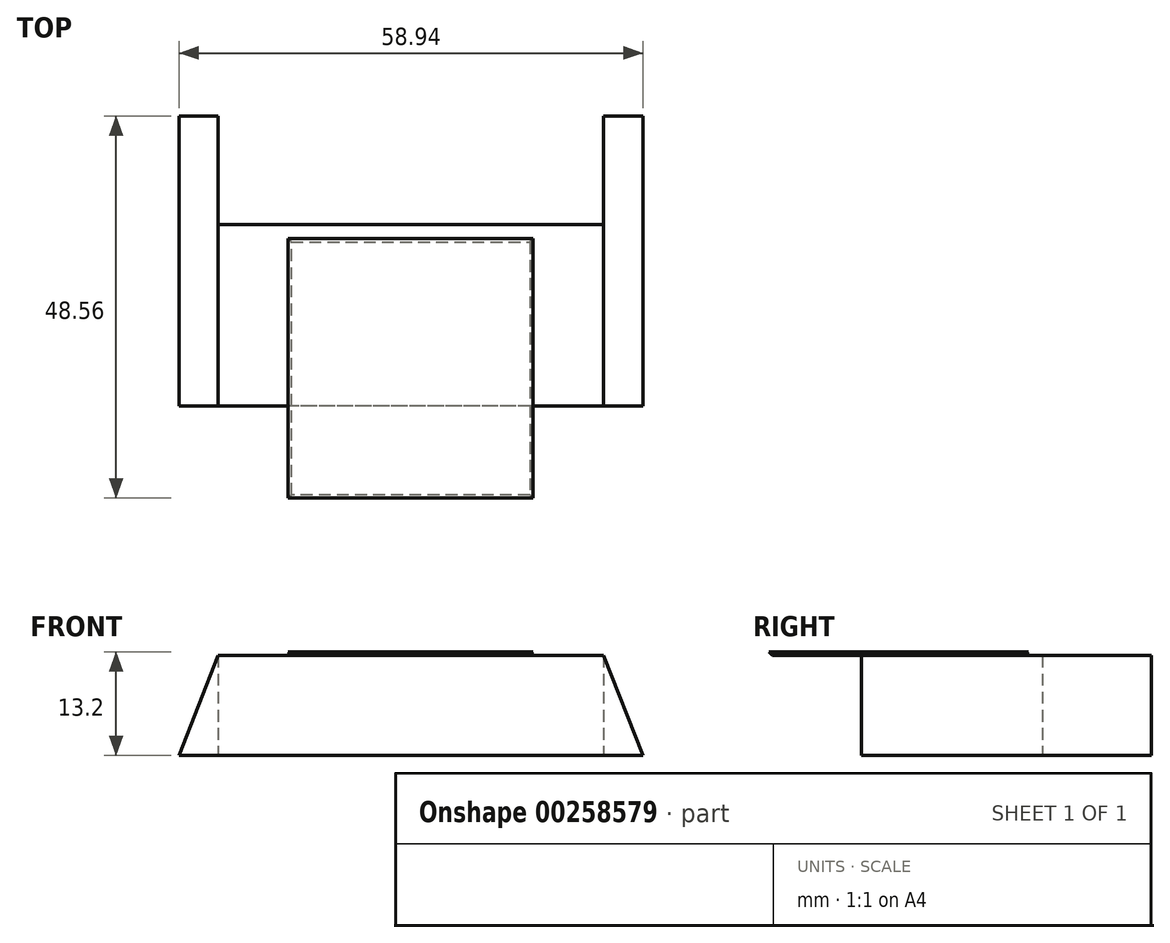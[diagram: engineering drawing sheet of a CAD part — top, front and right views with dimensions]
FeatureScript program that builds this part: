
annotation { "Feature Type Name" : "Feature", "Feature Type Description" : "" }
export const myFeature = defineFeature(function(context is Context, id is Id, definition is map)
    precondition{}
    {
        {
            var Q0;
            Q0=qCreatedBy(makeId("Top.planeOp"),FACE);
            var sketch = newSketch(context, id + "F0", { "sketchPlane" : qUnion([Q0])});
            skLineSegment(sketch, "E0.bottom", {"start": v(24.47, 23.01) * mm, "end": v(-24.47, 23.01) * mm});
            skLineSegment(sketch, "E0.top", {"start": v(24.47, -23.01) * mm, "end": v(-24.47, -23.01) * mm});
            skLineSegment(sketch, "E0.left", {"start": v(24.47, 23.01) * mm, "end": v(24.47, -23.01) * mm});
            skLineSegment(sketch, "E0.right", {"start": v(-24.47, 23.01) * mm, "end": v(-24.47, -23.01) * mm});
            skPoint(sketch, "E0.middle", {"position": v(0, 0) * mm});
            skLineSegment(sketch, "E1", {"start": v(-24.47, 0) * mm, "end": v(24.47, 0) * mm});
            skSolve(sketch);
        }
        {
            var Q0;
            {var subQ0=sQuery(id+"F0.wireOp",EDGE,"E0.top");Q0=makeQuery(id+"F0.imprint","IMPRINT",FACE,{"disambiguationData":[TD([[makeQuery(id+"F0.imprint","IMPRINT",EDGE,{"derivedFrom":subQ0}),-1.0]])]});}
            extrude(context, id + "F1", {"entities" : qUnion([Q0]), "depth" : 12.7 * mm});
        }
        {
            var Q0;
            Q0=makeQuery(id+"F1.opExtrude","SWEPT_FACE",FACE,{"disambiguationData":[OSD([sQuery(id+"F0.wireOp",EDGE,"E0.top")])]});
            var sketch = newSketch(context, id + "F2", { "sketchPlane" : qUnion([Q0])});
            skLineSegment(sketch, "E2", {"start": v(0, 12.7) * mm, "end": v(0, 0) * mm});
            skLineSegment(sketch, "E3.bottom", {"start": v(-29.47, 12.7) * mm, "end": v(29.47, 12.7) * mm});
            skLineSegment(sketch, "E3.top", {"start": v(-29.47, 0) * mm, "end": v(29.47, 0) * mm});
            skLineSegment(sketch, "E3.left", {"start": v(-29.47, 12.7) * mm, "end": v(-29.47, 0) * mm});
            skLineSegment(sketch, "E3.right", {"start": v(29.47, 12.7) * mm, "end": v(29.47, 0) * mm});
            skPoint(sketch, "E3.middle", {"position": v(0, 6.35) * mm});
            skLineSegment(sketch, "E4", {"start": v(-24.47, 12.7) * mm, "end": v(-29.47, 0) * mm});
            skLineSegment(sketch, "E5", {"start": v(24.47, 12.7) * mm, "end": v(29.47, 0) * mm});
            skSolve(sketch);
        }
        {
            var Q0;
            {var subQ2=sQuery(id+"F2.wireOp",EDGE,"E5");Q0=makeQuery(id+"F2.imprint","IMPRINT",FACE,{"disambiguationData":[TD([[makeQuery(id+"F2.imprint","IMPRINT",EDGE,{"derivedFrom":subQ2}),-1.0]])]});}
            var Q1;
            {var subQ2=sQuery(id+"F2.wireOp",EDGE,"E4");Q1=makeQuery(id+"F2.imprint","IMPRINT",FACE,{"disambiguationData":[TD([[makeQuery(id+"F2.imprint","IMPRINT",EDGE,{"derivedFrom":subQ2}),1.0]])]});}
            extrude(context, id + "F3", {"entities" : qUnion([Q0, Q1]), "operationType" : NewBodyOperationType.ADD, "oppositeDirection" : true, "depth" : 36.83 * mm});
        }
        {
            var Q0;
            Q0=makeQuery(id+"F1.opExtrude","CAP_FACE",FACE,{"disambiguationData":[OSD([sQuery(id+"F0.wireOp",EDGE,"E0.top"),sQuery(id+"F0.wireOp",EDGE,"E0.left"),sQuery(id+"F0.wireOp",EDGE,"E0.right"),sQuery(id+"F0.wireOp",EDGE,"E1")])],"isStart":false});
            var sketch = newSketch(context, id + "F4", { "sketchPlane" : qUnion([Q0])});
            skLineSegment(sketch, "E6.bottom", {"start": v(-15.2, -34.32) * mm, "end": v(15.1, -34.32) * mm});
            skLineSegment(sketch, "E6.top", {"start": v(-15.2, -2.2) * mm, "end": v(15.1, -2.2) * mm});
            skLineSegment(sketch, "E6.left", {"start": v(-15.2, -34.32) * mm, "end": v(-15.2, -2.2) * mm});
            skLineSegment(sketch, "E6.right", {"start": v(15.1, -34.32) * mm, "end": v(15.1, -2.2) * mm});
            skSolve(sketch);
        }
        {
            var Q0;
            Q0 = qSketchRegion(id + "F4", true);
            extrude(context, id + "F5", {"entities" : qUnion([Q0]), "operationType" : NewBodyOperationType.ADD, "depth" : 0.5 * mm, "hasDraft" : true, "draftAngle" : 40 * degree});
        }
        {
            var Q0;
            Q0=makeQuery(id+"F5.opExtrude","CAP_FACE",FACE,{"disambiguationData":[OSD([sQuery(id+"F4.wireOp",EDGE,"E6.bottom"),sQuery(id+"F4.wireOp",EDGE,"E6.top"),sQuery(id+"F4.wireOp",EDGE,"E6.left"),sQuery(id+"F4.wireOp",EDGE,"E6.right")])],"isStart":false});
            var sketch = newSketch(context, id + "F6", { "sketchPlane" : qUnion([Q0])});
            skLineSegment(sketch, "E7", {"start": v(-15.61, -33.37) * mm, "end": v(15.51, -33.37) * mm});
            skLineSegment(sketch, "E8", {"start": v(15.51, -33.37) * mm, "end": v(15.51, -31.93) * mm});
            skLineSegment(sketch, "E9", {"start": v(15.51, -31.93) * mm, "end": v(-15.61, -31.93) * mm});
            skLineSegment(sketch, "E10", {"start": v(-15.61, -31.93) * mm, "end": v(-15.61, -30.6) * mm});
            skLineSegment(sketch, "E11", {"start": v(-15.61, -30.6) * mm, "end": v(15.51, -30.6) * mm});
            skLineSegment(sketch, "E12", {"start": v(15.51, -30.6) * mm, "end": v(15.51, -29.26) * mm});
            skLineSegment(sketch, "E13", {"start": v(15.51, -29.26) * mm, "end": v(-15.61, -29.26) * mm});
            skLineSegment(sketch, "E14", {"start": v(-15.61, -29.26) * mm, "end": v(-15.61, -27.92) * mm});
            skLineSegment(sketch, "E15", {"start": v(-15.61, -27.92) * mm, "end": v(15.51, -27.92) * mm});
            skLineSegment(sketch, "E16", {"start": v(15.51, -27.92) * mm, "end": v(15.51, -26.57) * mm});
            skLineSegment(sketch, "E17", {"start": v(15.51, -26.57) * mm, "end": v(-15.61, -26.57) * mm});
            skLineSegment(sketch, "E18", {"start": v(-15.61, -26.57) * mm, "end": v(-15.61, -23.29) * mm});
            skLineSegment(sketch, "E19", {"start": v(-15.61, -23.29) * mm, "end": v(15.51, -23.29) * mm});
            skLineSegment(sketch, "E20", {"start": v(-15.61, -24.97) * mm, "end": v(-15.61, -23.29) * mm});
            skLineSegment(sketch, "E21", {"start": v(-15.61, -24.97) * mm, "end": v(15.51, -24.97) * mm});
            skLineSegment(sketch, "E22", {"start": v(15.51, -24.97) * mm, "end": v(15.51, -23.29) * mm});
            skLineSegment(sketch, "E23", {"start": v(15.51, -23.29) * mm, "end": v(-15.61, -23.29) * mm});
            skLineSegment(sketch, "E24", {"start": v(-15.61, -23.29) * mm, "end": v(-15.61, -21.61) * mm});
            skLineSegment(sketch, "E25", {"start": v(-15.61, -21.61) * mm, "end": v(15.51, -21.61) * mm});
            skLineSegment(sketch, "E26", {"start": v(-15.61, -19.94) * mm, "end": v(15.51, -19.94) * mm});
            skLineSegment(sketch, "E27", {"start": v(15.51, -19.94) * mm, "end": v(15.51, -21.61) * mm});
            skLineSegment(sketch, "E28", {"start": v(-15.61, -18.26) * mm, "end": v(15.51, -18.26) * mm});
            skLineSegment(sketch, "E29", {"start": v(-15.61, -19.94) * mm, "end": v(-15.61, -18.26) * mm});
            skLineSegment(sketch, "E30", {"start": v(15.51, -17.04) * mm, "end": v(-15.61, -17.04) * mm});
            skLineSegment(sketch, "E31", {"start": v(-15.61, -17.04) * mm, "end": v(15.51, -17.04) * mm});
            skLineSegment(sketch, "E32", {"start": v(15.51, -18.26) * mm, "end": v(15.51, -17.04) * mm});
            skLineSegment(sketch, "E33", {"start": v(-15.61, -15.72) * mm, "end": v(-15.61, -17.04) * mm});
            skLineSegment(sketch, "E34", {"start": v(-15.61, -15.72) * mm, "end": v(15.51, -15.72) * mm});
            skLineSegment(sketch, "E35", {"start": v(15.51, -15.72) * mm, "end": v(15.51, -14.48) * mm});
            skLineSegment(sketch, "E36", {"start": v(15.51, -14.48) * mm, "end": v(-15.61, -14.48) * mm});
            skLineSegment(sketch, "E37", {"start": v(-15.61, -14.48) * mm, "end": v(-15.61, -13.04) * mm});
            skLineSegment(sketch, "E38", {"start": v(-15.61, -13.04) * mm, "end": v(15.51, -13.04) * mm});
            skLineSegment(sketch, "E39", {"start": v(15.51, -13.04) * mm, "end": v(15.51, -11.77) * mm});
            skLineSegment(sketch, "E40", {"start": v(15.51, -11.77) * mm, "end": v(-15.61, -11.77) * mm});
            skLineSegment(sketch, "E41", {"start": v(-15.61, -11.77) * mm, "end": v(-15.61, -10.55) * mm});
            skLineSegment(sketch, "E42", {"start": v(-15.61, -10.55) * mm, "end": v(15.51, -10.55) * mm});
            skLineSegment(sketch, "E43", {"start": v(15.51, -10.55) * mm, "end": v(15.51, -9.4) * mm});
            skLineSegment(sketch, "E44", {"start": v(15.51, -9.4) * mm, "end": v(-15.61, -9.4) * mm});
            skLineSegment(sketch, "E45", {"start": v(-15.61, -9.4) * mm, "end": v(-15.61, -8.3) * mm});
            skLineSegment(sketch, "E46", {"start": v(-15.61, -8.3) * mm, "end": v(15.51, -8.3) * mm});
            skLineSegment(sketch, "E47", {"start": v(15.51, -8.3) * mm, "end": v(15.51, -7.12) * mm});
            skLineSegment(sketch, "E48", {"start": v(15.51, -7.12) * mm, "end": v(-15.61, -7.12) * mm});
            skLineSegment(sketch, "E49", {"start": v(-15.61, -7.12) * mm, "end": v(-15.61, -5.93) * mm});
            skLineSegment(sketch, "E50", {"start": v(-15.61, -5.93) * mm, "end": v(15.51, -5.93) * mm});
            skLineSegment(sketch, "E51", {"start": v(15.51, -5.93) * mm, "end": v(15.51, -4.74) * mm});
            skLineSegment(sketch, "E52", {"start": v(15.51, -4.74) * mm, "end": v(-15.61, -4.74) * mm});
            skLineSegment(sketch, "E53", {"start": v(-15.61, -4.74) * mm, "end": v(-15.61, -3.46) * mm});
            skLineSegment(sketch, "E54", {"start": v(-15.61, -3.46) * mm, "end": v(15.51, -3.46) * mm});
            skLineSegment(sketch, "E55", {"start": v(15.51, -3.46) * mm, "end": v(15.51, -1.78) * mm});
            skLineSegment(sketch, "E56", {"start": v(15.51, -1.78) * mm, "end": v(-15.61, -1.78) * mm});
            skSolve(sketch);
        }
        {
            var Q0;
            Q0 = qSketchRegion(id + "F6", true);
            var Q1;
            Q1=sQuery(id+"F6.wireOp",EDGE,"E9");
            var Q2;
            Q2=sQuery(id+"F6.wireOp",EDGE,"E11");
            var Q3;
            Q3=sQuery(id+"F6.wireOp",EDGE,"E13");
            var Q4;
            Q4=sQuery(id+"F6.wireOp",EDGE,"E17");
            var Q5;
            Q5=sQuery(id+"F6.wireOp",EDGE,"E15");
            var Q6;
            Q6=sQuery(id+"F6.wireOp",EDGE,"E21");
            var Q7;
            Q7=sQuery(id+"F6.wireOp",EDGE,"E25");
            var Q8;
            Q8=sQuery(id+"F6.wireOp",EDGE,"E23");
            var Q9;
            Q9=sQuery(id+"F6.wireOp",EDGE,"E26");
            var Q10;
            Q10=sQuery(id+"F6.wireOp",EDGE,"E31");
            var Q11;
            Q11=sQuery(id+"F6.wireOp",EDGE,"E28");
            var Q12;
            Q12=sQuery(id+"F6.wireOp",EDGE,"E34");
            var Q13;
            Q13=sQuery(id+"F6.wireOp",EDGE,"E36");
            var Q14;
            Q14=sQuery(id+"F6.wireOp",EDGE,"E38");
            var Q15;
            Q15=sQuery(id+"F6.wireOp",EDGE,"E40");
            var Q16;
            Q16=sQuery(id+"F6.wireOp",EDGE,"E42");
            var Q17;
            Q17=sQuery(id+"F6.wireOp",EDGE,"E46");
            var Q18;
            Q18=sQuery(id+"F6.wireOp",EDGE,"E44");
            var Q19;
            Q19=sQuery(id+"F6.wireOp",EDGE,"E48");
            var Q20;
            Q20=sQuery(id+"F6.wireOp",EDGE,"E50");
            var Q21;
            Q21=sQuery(id+"F6.wireOp",EDGE,"E52");
            var Q22;
            Q22=sQuery(id+"F6.wireOp",EDGE,"E54");
            var Q23;
            Q23=sQuery(id+"F6.wireOp",EDGE,"E56");
            var Q24;
            Q24=sQuery(id+"F6.wireOp",EDGE,"E7");
            extrude(context, id + "F7", {"entities" : qUnion([Q0]), "bodyType" : ToolBodyType.SURFACE, "surfaceEntities" : qUnion([Q1, Q2, Q3, Q4, Q5, Q6, Q7, Q8, Q9, Q10, Q11, Q12, Q13, Q14, Q15, Q16, Q17, Q18, Q19, Q20, Q21, Q22, Q23, Q24]), "depth" : 0.5 * mm});
        }
        {
            var Q0;
            Q0=makeQuery(id+"F1.opExtrude","CAP_FACE",FACE,{"disambiguationData":[OSD([sQuery(id+"F0.wireOp",EDGE,"E0.top"),sQuery(id+"F0.wireOp",EDGE,"E0.left"),sQuery(id+"F0.wireOp",EDGE,"E0.right"),sQuery(id+"F0.wireOp",EDGE,"E1")])],"isStart":false});
            var sketch = newSketch(context, id + "F8", { "sketchPlane" : qUnion([Q0])});
            skLineSegment(sketch, "E57.bottom", {"start": v(15.1, -2.2) * mm, "end": v(-15.2, -2.2) * mm});
            skLineSegment(sketch, "E57.top", {"start": v(15.1, -34.32) * mm, "end": v(-15.2, -34.32) * mm});
            skLineSegment(sketch, "E57.left", {"start": v(15.1, -2.2) * mm, "end": v(15.1, -34.32) * mm});
            skLineSegment(sketch, "E57.right", {"start": v(-15.2, -2.2) * mm, "end": v(-15.2, -34.32) * mm});
            skSolve(sketch);
        }
        {
            var Q0;
            Q0 = qSketchRegion(id + "F8", true);
            var Q1;
            Q1 = qBodyType(qCreatedBy(id + "F8" ,EDGE), BodyType.WIRE);
            extrude(context, id + "F9", {"entities" : qUnion([Q0]), "bodyType" : ToolBodyType.SURFACE, "surfaceEntities" : qUnion([Q1]), "depth" : 0.97 * mm});
        }
    });
